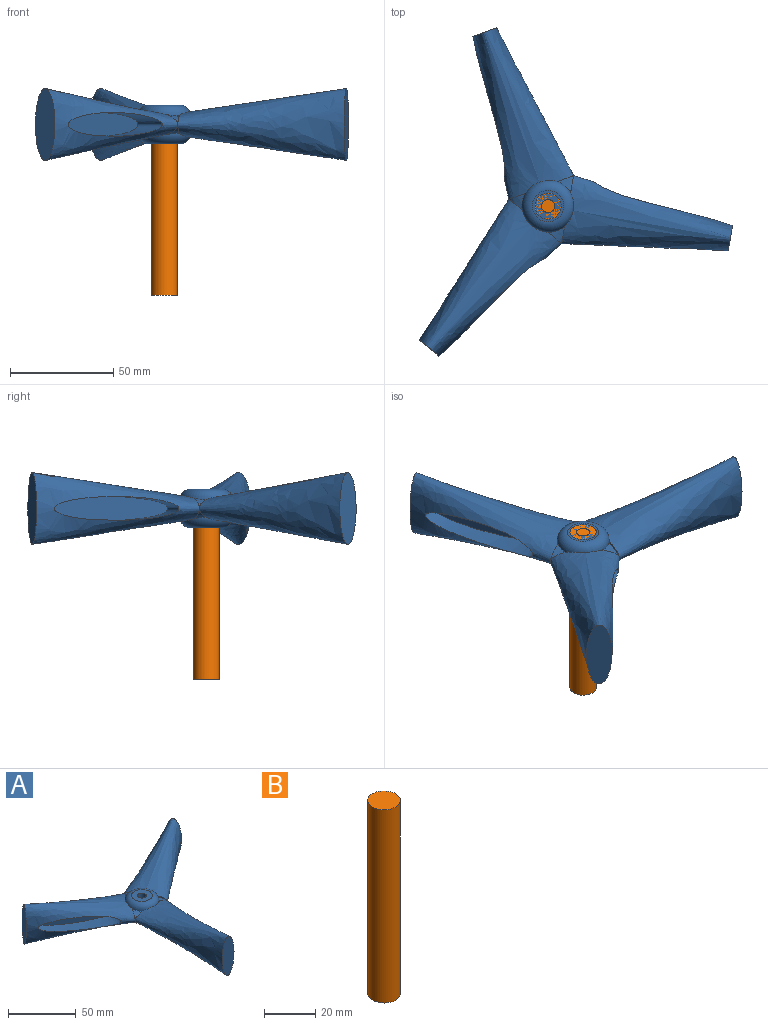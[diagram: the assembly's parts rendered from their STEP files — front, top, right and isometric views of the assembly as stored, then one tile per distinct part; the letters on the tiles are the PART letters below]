
ASSEMBLY  parts=2 mates=1
PART A: 42 faces, bbox 161.5x143.5x34.9 mm
  f0: torus R=7.6mm, axis (0,0,1), area 460.7mm2, adj f1,f3,f6,f8,f11,f13,f14,f18
  f1: plane 7.41x4.54mm, normal (-0.87,-0.5,0), area 7.6mm2, adj f0,f3,f18,f37
  f2: plane 7.41x4.54mm, normal (-0.87,-0.5,0), area 7.6mm2, adj f4,f5,f18,f35
  f3: cylinder r=12.68mm len=3.87mm, axis (0,0,-1), area 1mm2, adj f0,f1,f37
  f4: cylinder r=12.68mm len=3.87mm, axis (0,0,-1), area 1mm2, adj f2,f5,f35
  f5: torus R=7.6mm, axis (0,0,1), area 460.7mm2, adj f2,f4,f7,f9,f10,f12,f14,f18
  f6: cylinder r=12.68mm len=4.05mm, axis (0,0,-1), area 1mm2, adj f0,f8,f33
  f7: cylinder r=12.68mm len=4.05mm, axis (0,0,-1), area 1mm2, adj f5,f9,f32
  f8: plane 7.41x4.54mm, normal (-0.87,-0.5,0), area 7.6mm2, adj f0,f6,f18,f33
  f9: plane 7.41x4.54mm, normal (-0.87,-0.5,0), area 7.6mm2, adj f5,f7,f18,f32
  f10: cylinder r=12.68mm len=3.15mm, axis (0,0,-1), area 1mm2, adj f5,f12,f30
  f11: cylinder r=12.68mm len=3.15mm, axis (0,0,-1), area 1mm2, adj f0,f13,f31
  f12: plane 8.55x4.54mm, normal (0,1,0), area 7.6mm2, adj f5,f10,f14,f30
  f13: plane 8.55x4.54mm, normal (0,1,0), area 7.6mm2, adj f0,f11,f14,f31
  f14: bspline ~80.01x34.82mm, area 5272.3mm2, adj f0,f5,f12,f13,f15,f16,f18,f22
  f15: plane 34.82x12.32mm, normal (0,-1,0), area 336.8mm2, adj f14
  f16: extruded ~61.14x15.4mm, area 1310.5mm2, adj f14,f17
  f17: plane 61.14x11.71mm, normal (1,0,0), area 562.5mm2, adj f16
  f18: bspline ~80.74x59.83mm, area 5272.3mm2, adj f0,f1,f2,f5,f8,f9,f14,f19
  f19: plane 34.82x10.67mm, normal (0.87,0.5,0), area 336.8mm2, adj f18
  f20: extruded ~60.65x43.91mm, area 1291.7mm2, adj f18,f21,f38,f39,f40,f41
  f21: plane 52.95x30.57mm, normal (-0.5,0.87,0), area 562.5mm2, adj f20
  f22: bspline ~80.74x59.83mm, area 5272.3mm2, adj f0,f5,f14,f18,f23,f24,f29,f30
  f23: plane 34.82x10.67mm, normal (-0.87,0.5,0), area 336.8mm2, adj f22
  f24: extruded ~60.65x43.91mm, area 1310.5mm2, adj f22,f25
  f25: plane 52.95x30.57mm, normal (-0.5,-0.87,0), area 562.5mm2, adj f24
  f26: cylinder r=3.17mm len=18.8mm, axis (0,0,-1), area 375mm2, adj f27,f28
  f27: plane 15.2x15.2mm, normal (0,0,1), area 149.7mm2, adj f5,f26
  f28: plane 15.2x15.2mm, normal (0,0,-1), area 149.7mm2, adj f0,f26
  f29: plane 0.1x0.05mm, normal (-0.1,-0.16,0.98), area 0mm2, adj f5,f22,f30
  f30: extruded ~10.93x10.52mm, area 29.6mm2, adj f5,f10,f12,f22,f29
  f31: extruded ~11x10.56mm, area 29.6mm2, adj f0,f11,f13,f22
  f32: extruded ~11x10.56mm, area 29.6mm2, adj f5,f7,f9,f22
  f33: extruded ~10.93x10.52mm, area 29.6mm2, adj f0,f6,f8,f22,f34
  f34: plane 0.1x0.07mm, normal (0.09,0.16,-0.98), area 0mm2, adj f0,f22,f33
  f35: extruded ~8.42x7.29mm, area 29.6mm2, adj f2,f4,f5,f14,f36
  f36: plane 0.08x0.06mm, normal (0.19,0,0.98), area 0mm2, adj f5,f14,f35
  f37: extruded ~8.49x7.29mm, area 29.6mm2, adj f0,f1,f3,f14
  f38: plane 5.22x1.21mm, normal (1,0,0), area 5.5mm2, adj f20,f39,f40,f41
  f39: plane 4.07x3.09mm, normal (0,1,0), area 7.9mm2, adj f20,f38,f40,f41
  f40: extruded ~4.84x1.41mm, area 4.1mm2, adj f20,f38,f39
  f41: extruded ~4.84x1.41mm, area 4.1mm2, adj f20,f38,f39
PART B: 3 faces, bbox 12.7x12.7x92.2 mm
  f0: cylinder r=6.35mm len=92.2mm, axis (0,0,-1), area 3678.7mm2, adj f1,f2
  f1: plane 12.7x12.7mm, normal (0,0,1), area 126.7mm2, adj f0
  f2: plane 12.7x12.7mm, normal (0,0,-1), area 126.7mm2, adj f0
PLACE A rot(axis=(0,0,-1),40deg) t=(-43.75,18.13,65.08)mm
PLACE B t=(-37.56,25.5,-17.73)mm fixed
MATE revolute B.f0 <-> A.f0  axis (0,0,1) through (-37.56,25.5,74.48)mm
